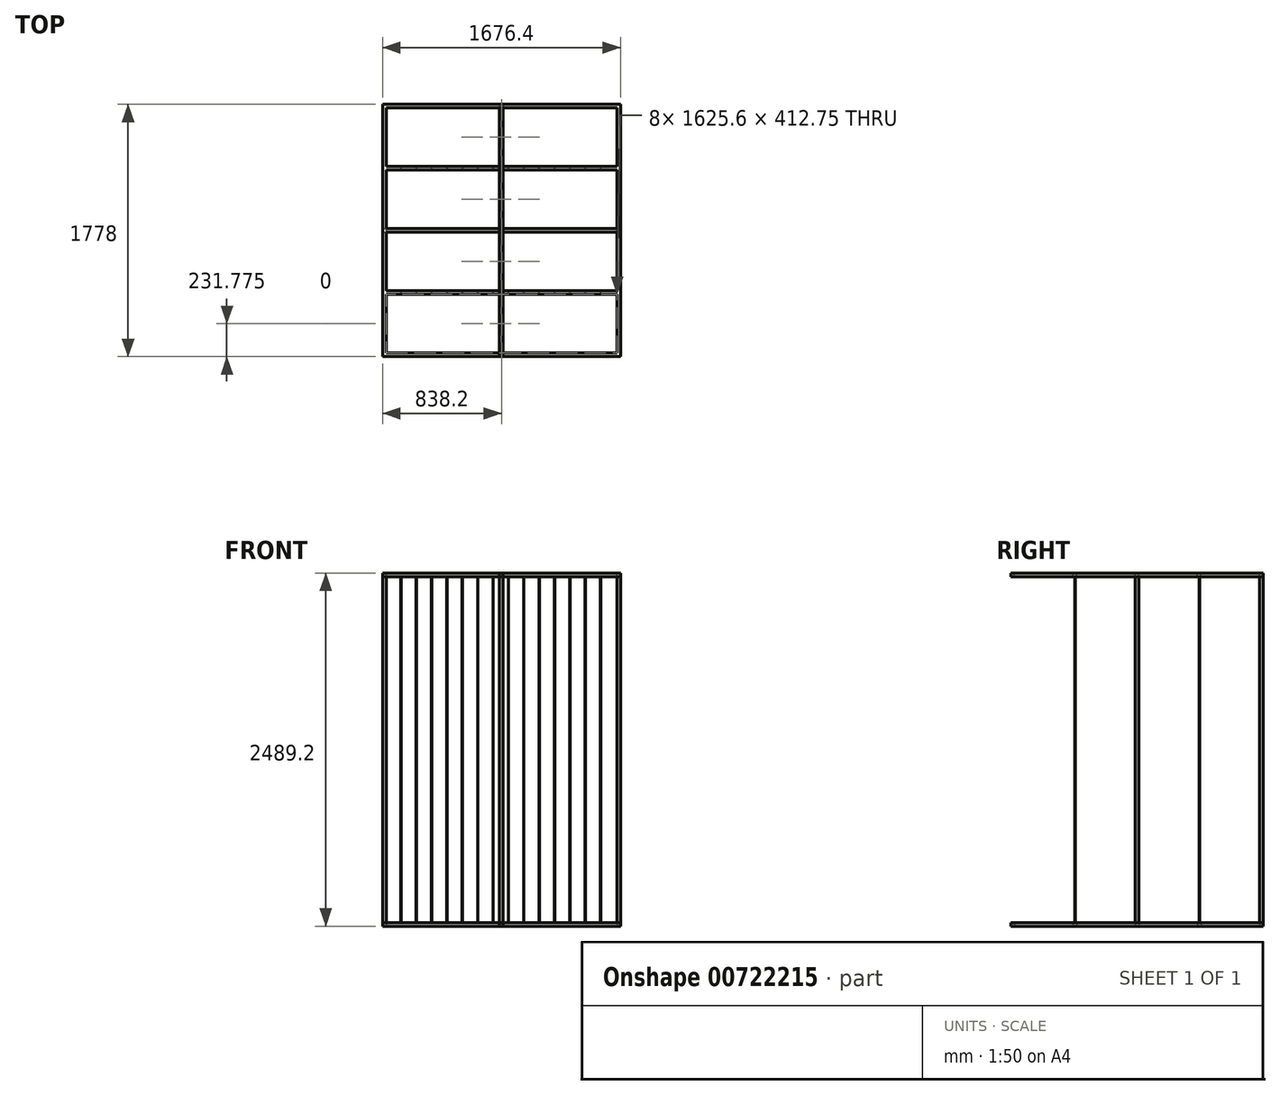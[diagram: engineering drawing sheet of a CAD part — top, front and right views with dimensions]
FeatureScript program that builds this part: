
annotation { "Feature Type Name" : "Feature", "Feature Type Description" : "" }
export const myFeature = defineFeature(function(context is Context, id is Id, definition is map)
    precondition{}
    {
        {
            var Q0;
            Q0=qCreatedBy(makeId("Top.planeOp"),FACE);
            var sketch = newSketch(context, id + "F0", { "sketchPlane" : qUnion([Q0])});
            skLineSegment(sketch, "E0.bottom", {"start": v(838.2, -889) * mm, "end": v(-838.2, -889) * mm});
            skLineSegment(sketch, "E0.top", {"start": v(838.2, 889) * mm, "end": v(-838.2, 889) * mm});
            skLineSegment(sketch, "E0.left", {"start": v(838.2, -889) * mm, "end": v(838.2, 889) * mm});
            skLineSegment(sketch, "E0.right", {"start": v(-838.2, -889) * mm, "end": v(-838.2, 889) * mm});
            skPoint(sketch, "E0.middle", {"position": v(0, 0) * mm});
            skLineSegment(sketch, "E1.0", {"start": v(812.8, 863.6) * mm, "end": v(-812.8, 863.6) * mm});
            skLineSegment(sketch, "E1.1", {"start": v(812.8, -863.6) * mm, "end": v(812.8, -450.85) * mm});
            skLineSegment(sketch, "E1.2", {"start": v(812.8, -863.6) * mm, "end": v(-812.8, -863.6) * mm});
            skLineSegment(sketch, "E1.3", {"start": v(-812.8, -863.6) * mm, "end": v(-812.8, -450.85) * mm});
            skLineSegment(sketch, "E2", {"start": v(-812.8, -450.85) * mm, "end": v(812.8, -450.85) * mm});
            skLineSegment(sketch, "E3", {"start": v(812.8, -425.45) * mm, "end": v(-812.8, -425.45) * mm});
            skLineSegment(sketch, "E4", {"start": v(-812.8, -12.7) * mm, "end": v(812.8, -12.7) * mm});
            skLineSegment(sketch, "E5", {"start": v(-812.8, 0) * mm, "end": v(812.8, 0) * mm, "construction": true});
            skLineSegment(sketch, "E6.MirrorCS", {"start": v(-812.8, 12.7) * mm, "end": v(812.8, 12.7) * mm});
            skLineSegment(sketch, "E7.MirrorCS", {"start": v(812.8, 425.45) * mm, "end": v(-812.8, 425.45) * mm});
            skLineSegment(sketch, "E8.MirrorCS", {"start": v(-812.8, 450.85) * mm, "end": v(812.8, 450.85) * mm});
            skLineSegment(sketch, "E9.trimOffspring", {"start": v(812.8, 450.85) * mm, "end": v(812.8, 863.6) * mm});
            skLineSegment(sketch, "E10.trimOffspring", {"start": v(812.8, 12.7) * mm, "end": v(812.8, 425.45) * mm});
            skLineSegment(sketch, "E11.trimOffspring", {"start": v(812.8, -425.45) * mm, "end": v(812.8, -12.7) * mm});
            skLineSegment(sketch, "E12.trimOffspring", {"start": v(-812.8, -425.45) * mm, "end": v(-812.8, -12.7) * mm});
            skLineSegment(sketch, "E13.trimOffspring", {"start": v(-812.8, 12.7) * mm, "end": v(-812.8, 425.45) * mm});
            skLineSegment(sketch, "E14.trimOffspring", {"start": v(-812.8, 450.85) * mm, "end": v(-812.8, 863.6) * mm});
            skSolve(sketch);
        }
        {
            var Q0;
            Q0 = qSketchRegion(id + "F0", true);
            extrude(context, id + "F1", {"entities" : qUnion([Q0]), "depth" : 25.4 * mm, "offsetDistance" : 25.4 * mm});
        }
        {
            var Q0;
            Q0=qCreatedBy(makeId("Top.planeOp"),FACE);
            cPlane(context, id + "F2", {"entities" : qUnion([Q0]), "cplaneType" : CPlaneType.OFFSET, "offset" : 1244.6 * mm, "width" : 152.4 * mm, "height" : 152.4 * mm});
        }
        {
            var Q0;
            Q0=makeQuery(id+"F1.opExtrude","SWEPT_BODY",BODY,{"disambiguationData":[OSD([sQuery(id+"F0.wireOp",EDGE,"E0.bottom"),sQuery(id+"F0.wireOp",EDGE,"E0.top"),sQuery(id+"F0.wireOp",EDGE,"E0.left"),sQuery(id+"F0.wireOp",EDGE,"E0.right"),sQuery(id+"F0.wireOp",EDGE,"E1.0"),sQuery(id+"F0.wireOp",EDGE,"E1.1"),sQuery(id+"F0.wireOp",EDGE,"E1.2"),sQuery(id+"F0.wireOp",EDGE,"E1.3"),sQuery(id+"F0.wireOp",EDGE,"E2"),sQuery(id+"F0.wireOp",EDGE,"E3"),sQuery(id+"F0.wireOp",EDGE,"E4"),sQuery(id+"F0.wireOp",EDGE,"E6.MirrorCS"),sQuery(id+"F0.wireOp",EDGE,"E7.MirrorCS"),sQuery(id+"F0.wireOp",EDGE,"E8.MirrorCS"),sQuery(id+"F0.wireOp",EDGE,"E9.trimOffspring"),sQuery(id+"F0.wireOp",EDGE,"E10.trimOffspring"),sQuery(id+"F0.wireOp",EDGE,"E11.trimOffspring"),sQuery(id+"F0.wireOp",EDGE,"E12.trimOffspring"),sQuery(id+"F0.wireOp",EDGE,"E13.trimOffspring"),sQuery(id+"F0.wireOp",EDGE,"E14.trimOffspring")])]});
            var Q1;
            Q1=qCreatedBy(id+"F2.planeOp",FACE);
            mirror(context, id + "F3", {"entities" : qUnion([Q0]), "mirrorPlane" : qUnion([Q1])});
        }
        {
            var Q0;
            Q0=makeQuery(id+"F1.opExtrude","CAP_FACE",FACE,{"disambiguationData":[OSD([sQuery(id+"F0.wireOp",EDGE,"E0.bottom"),sQuery(id+"F0.wireOp",EDGE,"E0.top"),sQuery(id+"F0.wireOp",EDGE,"E0.left"),sQuery(id+"F0.wireOp",EDGE,"E0.right"),sQuery(id+"F0.wireOp",EDGE,"E1.0"),sQuery(id+"F0.wireOp",EDGE,"E1.1"),sQuery(id+"F0.wireOp",EDGE,"E1.2"),sQuery(id+"F0.wireOp",EDGE,"E1.3"),sQuery(id+"F0.wireOp",EDGE,"E2"),sQuery(id+"F0.wireOp",EDGE,"E3"),sQuery(id+"F0.wireOp",EDGE,"E4"),sQuery(id+"F0.wireOp",EDGE,"E6.MirrorCS"),sQuery(id+"F0.wireOp",EDGE,"E7.MirrorCS"),sQuery(id+"F0.wireOp",EDGE,"E8.MirrorCS"),sQuery(id+"F0.wireOp",EDGE,"E9.trimOffspring"),sQuery(id+"F0.wireOp",EDGE,"E10.trimOffspring"),sQuery(id+"F0.wireOp",EDGE,"E11.trimOffspring"),sQuery(id+"F0.wireOp",EDGE,"E12.trimOffspring"),sQuery(id+"F0.wireOp",EDGE,"E13.trimOffspring"),sQuery(id+"F0.wireOp",EDGE,"E14.trimOffspring")])],"isStart":false});
            var sketch = newSketch(context, id + "F4", { "sketchPlane" : qUnion([Q0])});
            skLineSegment(sketch, "E15.0", {"start": v(838.2, 889) * mm, "end": v(-838.2, 889) * mm});
            skLineSegment(sketch, "E15.1", {"start": v(-838.2, -889) * mm, "end": v(-838.2, 889) * mm});
            skLineSegment(sketch, "E15.2", {"start": v(838.2, -889) * mm, "end": v(838.2, 889) * mm});
            skLineSegment(sketch, "E15.3", {"start": v(838.2, -889) * mm, "end": v(-838.2, -889) * mm});
            skLineSegment(sketch, "E16.bottom", {"start": v(-838.2, -889) * mm, "end": v(-812.8, -889) * mm});
            skLineSegment(sketch, "E16.top", {"start": v(-838.2, -863.6) * mm, "end": v(-812.8, -863.6) * mm});
            skLineSegment(sketch, "E16.left", {"start": v(-838.2, -889) * mm, "end": v(-838.2, -863.6) * mm});
            skLineSegment(sketch, "E16.right", {"start": v(-812.8, -889) * mm, "end": v(-812.8, -863.6) * mm});
            skLineSegment(sketch, "E17.bottom", {"start": v(838.2, -889) * mm, "end": v(812.8, -889) * mm});
            skLineSegment(sketch, "E17.top", {"start": v(838.2, -863.6) * mm, "end": v(812.8, -863.6) * mm});
            skLineSegment(sketch, "E17.left", {"start": v(838.2, -889) * mm, "end": v(838.2, -863.6) * mm});
            skLineSegment(sketch, "E17.right", {"start": v(812.8, -889) * mm, "end": v(812.8, -863.6) * mm});
            skLineSegment(sketch, "E18.bottom", {"start": v(-838.2, 889) * mm, "end": v(-812.8, 889) * mm});
            skLineSegment(sketch, "E18.top", {"start": v(-838.2, 863.6) * mm, "end": v(-812.8, 863.6) * mm});
            skLineSegment(sketch, "E18.left", {"start": v(-838.2, 889) * mm, "end": v(-838.2, 863.6) * mm});
            skLineSegment(sketch, "E18.right", {"start": v(-812.8, 889) * mm, "end": v(-812.8, 863.6) * mm});
            skLineSegment(sketch, "E19.bottom", {"start": v(838.2, 889) * mm, "end": v(812.8, 889) * mm});
            skLineSegment(sketch, "E19.top", {"start": v(838.2, 863.6) * mm, "end": v(812.8, 863.6) * mm});
            skLineSegment(sketch, "E19.left", {"start": v(838.2, 889) * mm, "end": v(838.2, 863.6) * mm});
            skLineSegment(sketch, "E19.right", {"start": v(812.8, 889) * mm, "end": v(812.8, 863.6) * mm});
            skLineSegment(sketch, "E20.bottom", {"start": v(-812.8, 12.7) * mm, "end": v(-838.2, 12.7) * mm});
            skLineSegment(sketch, "E20.top", {"start": v(-812.8, -12.7) * mm, "end": v(-838.2, -12.7) * mm});
            skLineSegment(sketch, "E20.left", {"start": v(-812.8, 12.7) * mm, "end": v(-812.8, -12.7) * mm});
            skLineSegment(sketch, "E20.right", {"start": v(-838.2, 12.7) * mm, "end": v(-838.2, -12.7) * mm});
            skLineSegment(sketch, "E21.bottom", {"start": v(812.8, 12.7) * mm, "end": v(838.2, 12.7) * mm});
            skLineSegment(sketch, "E21.top", {"start": v(812.8, -12.7) * mm, "end": v(838.2, -12.7) * mm});
            skLineSegment(sketch, "E21.left", {"start": v(812.8, 12.7) * mm, "end": v(812.8, -12.7) * mm});
            skLineSegment(sketch, "E21.right", {"start": v(838.2, 12.7) * mm, "end": v(838.2, -12.7) * mm});
            skLineSegment(sketch, "E22.bottom", {"start": v(-12.7, 863.6) * mm, "end": v(12.7, 863.6) * mm});
            skLineSegment(sketch, "E22.top", {"start": v(-12.7, 889) * mm, "end": v(12.7, 889) * mm});
            skLineSegment(sketch, "E22.left", {"start": v(-12.7, 863.6) * mm, "end": v(-12.7, 889) * mm});
            skLineSegment(sketch, "E22.right", {"start": v(12.7, 863.6) * mm, "end": v(12.7, 889) * mm});
            skPoint(sketch, "E22.middle", {"position": v(0, 876.3) * mm});
            skPoint(sketch, "E22.middle.positionSnap0", {"position": v(0, 889) * mm});
            skPoint(sketch, "E22.middle.positionSnap1", {"position": v(-812.8, 876.3) * mm});
            skPoint(sketch, "E22.centerSnap0", {"position": v(0, 889) * mm});
            skPoint(sketch, "E22.centerSnap1", {"position": v(-812.8, 876.3) * mm});
            skLineSegment(sketch, "E23.bottom", {"start": v(-12.7, -889) * mm, "end": v(12.7, -889) * mm});
            skLineSegment(sketch, "E23.top", {"start": v(-12.7, -863.6) * mm, "end": v(12.7, -863.6) * mm});
            skLineSegment(sketch, "E23.left", {"start": v(-12.7, -889) * mm, "end": v(-12.7, -863.6) * mm});
            skLineSegment(sketch, "E23.right", {"start": v(12.7, -889) * mm, "end": v(12.7, -863.6) * mm});
            skPoint(sketch, "E23.middle", {"position": v(0, -876.3) * mm});
            skPoint(sketch, "E23.middle.positionSnap0", {"position": v(0, -889) * mm});
            skPoint(sketch, "E23.middle.positionSnap1", {"position": v(-812.8, -876.3) * mm});
            skPoint(sketch, "E23.centerSnap0", {"position": v(0, -889) * mm});
            skPoint(sketch, "E23.centerSnap1", {"position": v(-812.8, -876.3) * mm});
            skSolve(sketch);
        }
        {
            var Q0;
            Q0=makeQuery(id+"F4.imprint","IMPRINT",FACE,{"disambiguationData":[TD([[makeQuery(id+"F4.imprint","IMPRINT",EDGE,{"derivedFrom":sQuery(id+"F4.wireOp",EDGE,"E20.bottom")}),1.0]])]});
            var Q1;
            Q1=makeQuery(id+"F4.imprint","IMPRINT",FACE,{"disambiguationData":[TD([[makeQuery(id+"F4.imprint","IMPRINT",EDGE,{"derivedFrom":sQuery(id+"F4.wireOp",EDGE,"E18.bottom")}),1.0]])]});
            var Q2;
            Q2=makeQuery(id+"F4.imprint","IMPRINT",FACE,{"disambiguationData":[TD([[makeQuery(id+"F4.imprint","IMPRINT",EDGE,{"derivedFrom":sQuery(id+"F4.wireOp",EDGE,"E22.bottom")}),-1.0]])]});
            var Q3;
            Q3=makeQuery(id+"F4.imprint","IMPRINT",FACE,{"disambiguationData":[TD([[makeQuery(id+"F4.imprint","IMPRINT",EDGE,{"derivedFrom":sQuery(id+"F4.wireOp",EDGE,"E19.bottom")}),1.0]])]});
            var Q4;
            Q4=makeQuery(id+"F4.imprint","IMPRINT",FACE,{"disambiguationData":[TD([[makeQuery(id+"F4.imprint","IMPRINT",EDGE,{"derivedFrom":sQuery(id+"F4.wireOp",EDGE,"E21.bottom")}),-1.0]])]});
            var Q5;
            Q5=makeQuery(id+"F4.imprint","IMPRINT",FACE,{"disambiguationData":[TD([[makeQuery(id+"F4.imprint","IMPRINT",EDGE,{"derivedFrom":sQuery(id+"F4.wireOp",EDGE,"E17.bottom")}),-1.0]])]});
            var Q6;
            Q6=makeQuery(id+"F4.imprint","IMPRINT",FACE,{"disambiguationData":[TD([[makeQuery(id+"F4.imprint","IMPRINT",EDGE,{"derivedFrom":sQuery(id+"F4.wireOp",EDGE,"E23.bottom")}),-1.0]])]});
            var Q7;
            Q7=makeQuery(id+"F4.imprint","IMPRINT",FACE,{"disambiguationData":[TD([[makeQuery(id+"F4.imprint","IMPRINT",EDGE,{"derivedFrom":sQuery(id+"F4.wireOp",EDGE,"E16.bottom")}),-1.0]])]});
            var Q8;
            Q8=makeQuery(id+"F1.opExtrude","CAP_FACE",FACE,{"disambiguationData":[OSD([sQuery(id+"F0.wireOp",EDGE,"E0.bottom"),sQuery(id+"F0.wireOp",EDGE,"E0.top"),sQuery(id+"F0.wireOp",EDGE,"E0.left"),sQuery(id+"F0.wireOp",EDGE,"E0.right"),sQuery(id+"F0.wireOp",EDGE,"E1.0"),sQuery(id+"F0.wireOp",EDGE,"E1.1"),sQuery(id+"F0.wireOp",EDGE,"E1.2"),sQuery(id+"F0.wireOp",EDGE,"E1.3"),sQuery(id+"F0.wireOp",EDGE,"E2"),sQuery(id+"F0.wireOp",EDGE,"E3"),sQuery(id+"F0.wireOp",EDGE,"E4"),sQuery(id+"F0.wireOp",EDGE,"E6.MirrorCS"),sQuery(id+"F0.wireOp",EDGE,"E7.MirrorCS"),sQuery(id+"F0.wireOp",EDGE,"E8.MirrorCS"),sQuery(id+"F0.wireOp",EDGE,"E9.trimOffspring"),sQuery(id+"F0.wireOp",EDGE,"E10.trimOffspring"),sQuery(id+"F0.wireOp",EDGE,"E11.trimOffspring"),sQuery(id+"F0.wireOp",EDGE,"E12.trimOffspring"),sQuery(id+"F0.wireOp",EDGE,"E13.trimOffspring"),sQuery(id+"F0.wireOp",EDGE,"E14.trimOffspring")])],"isStart":false});
            var Q9;
            Q9=makeQuery(id+"F3.opPattern","COPY",BODY,{"derivedFrom":makeQuery(id+"F1.opExtrude","SWEPT_BODY",BODY,{"disambiguationData":[OSD([sQuery(id+"F0.wireOp",EDGE,"E0.bottom"),sQuery(id+"F0.wireOp",EDGE,"E0.top"),sQuery(id+"F0.wireOp",EDGE,"E0.left"),sQuery(id+"F0.wireOp",EDGE,"E0.right"),sQuery(id+"F0.wireOp",EDGE,"E1.0"),sQuery(id+"F0.wireOp",EDGE,"E1.1"),sQuery(id+"F0.wireOp",EDGE,"E1.2"),sQuery(id+"F0.wireOp",EDGE,"E1.3"),sQuery(id+"F0.wireOp",EDGE,"E2"),sQuery(id+"F0.wireOp",EDGE,"E3"),sQuery(id+"F0.wireOp",EDGE,"E4"),sQuery(id+"F0.wireOp",EDGE,"E6.MirrorCS"),sQuery(id+"F0.wireOp",EDGE,"E7.MirrorCS"),sQuery(id+"F0.wireOp",EDGE,"E8.MirrorCS"),sQuery(id+"F0.wireOp",EDGE,"E9.trimOffspring"),sQuery(id+"F0.wireOp",EDGE,"E10.trimOffspring"),sQuery(id+"F0.wireOp",EDGE,"E11.trimOffspring"),sQuery(id+"F0.wireOp",EDGE,"E12.trimOffspring"),sQuery(id+"F0.wireOp",EDGE,"E13.trimOffspring"),sQuery(id+"F0.wireOp",EDGE,"E14.trimOffspring")])]}),"instanceName":"1"});
            extrude(context, id + "F5", {"entities" : qUnion([Q0, Q1, Q2, Q3, Q4, Q5, Q6, Q7]), "endBound" : BoundingType.UP_TO_BODY, "depth" : 25.4 * mm, "endBoundEntityFace" : qUnion([Q8]), "endBoundEntityBody" : qUnion([Q9]), "offsetDistance" : 25.4 * mm});
        }
        {
            var Q0;
            Q0=makeQuery(id+"F1.opExtrude","SWEPT_FACE",FACE,{"disambiguationData":[OSD([sQuery(id+"F0.wireOp",EDGE,"E0.bottom")])]});
            var sketch = newSketch(context, id + "F6", { "sketchPlane" : qUnion([Q0])});
            skLineSegment(sketch, "E24", {"start": v(0, 0) * mm, "end": v(0, 25.4) * mm, "construction": true});
            skLineSegment(sketch, "E25", {"start": v(-12.7, 0) * mm, "end": v(-12.7, 25.4) * mm});
            skLineSegment(sketch, "E26.MirrorCS", {"start": v(12.7, 0) * mm, "end": v(12.7, 25.4) * mm});
            skLineSegment(sketch, "E27", {"start": v(-12.7, 25.4) * mm, "end": v(12.7, 25.4) * mm});
            skLineSegment(sketch, "E28", {"start": v(-12.7, 0) * mm, "end": v(12.7, 0) * mm});
            skSolve(sketch);
        }
        {
            var Q0;
            Q0 = qSketchRegion(id + "F6", true);
            var Q1;
            Q1=makeQuery(id+"F1.opExtrude","SWEPT_FACE",FACE,{"disambiguationData":[OSD([sQuery(id+"F0.wireOp",EDGE,"E1.0")])]});
            extrude(context, id + "F7", {"entities" : qUnion([Q0]), "endBound" : BoundingType.UP_TO_SURFACE, "oppositeDirection" : true, "depth" : 25.4 * mm, "endBoundEntityFace" : qUnion([Q1]), "offsetDistance" : 25.4 * mm});
        }
        {
            var Q0;
            Q0=makeQuery(id+"F7.opExtrude","SWEPT_BODY",BODY,{"disambiguationData":[OSD([sQuery(id+"F6.wireOp",EDGE,"E25"),sQuery(id+"F6.wireOp",EDGE,"E26.MirrorCS"),sQuery(id+"F6.wireOp",EDGE,"E27"),sQuery(id+"F6.wireOp",EDGE,"E28")])]});
            var Q1;
            Q1=qCreatedBy(id+"F2.planeOp",FACE);
            mirror(context, id + "F8", {"entities" : qUnion([Q0]), "mirrorPlane" : qUnion([Q1])});
        }
        {
            var Q0;
            Q0=makeQuery(id+"F1.opExtrude","CAP_FACE",FACE,{"disambiguationData":[OSD([sQuery(id+"F0.wireOp",EDGE,"E0.bottom"),sQuery(id+"F0.wireOp",EDGE,"E0.top"),sQuery(id+"F0.wireOp",EDGE,"E0.left"),sQuery(id+"F0.wireOp",EDGE,"E0.right"),sQuery(id+"F0.wireOp",EDGE,"E1.0"),sQuery(id+"F0.wireOp",EDGE,"E1.1"),sQuery(id+"F0.wireOp",EDGE,"E1.2"),sQuery(id+"F0.wireOp",EDGE,"E1.3"),sQuery(id+"F0.wireOp",EDGE,"E2"),sQuery(id+"F0.wireOp",EDGE,"E3"),sQuery(id+"F0.wireOp",EDGE,"E4"),sQuery(id+"F0.wireOp",EDGE,"E6.MirrorCS"),sQuery(id+"F0.wireOp",EDGE,"E7.MirrorCS"),sQuery(id+"F0.wireOp",EDGE,"E8.MirrorCS"),sQuery(id+"F0.wireOp",EDGE,"E9.trimOffspring"),sQuery(id+"F0.wireOp",EDGE,"E10.trimOffspring"),sQuery(id+"F0.wireOp",EDGE,"E11.trimOffspring"),sQuery(id+"F0.wireOp",EDGE,"E12.trimOffspring"),sQuery(id+"F0.wireOp",EDGE,"E13.trimOffspring"),sQuery(id+"F0.wireOp",EDGE,"E14.trimOffspring")])],"isStart":false});
            var sketch = newSketch(context, id + "F9", { "sketchPlane" : qUnion([Q0])});
            skLineSegment(sketch, "E29.0", {"start": v(812.8, -425.45) * mm, "end": v(-812.8, -425.45) * mm, "construction": true});
            skLineSegment(sketch, "E29.1", {"start": v(-812.8, -450.85) * mm, "end": v(812.8, -450.85) * mm, "construction": true});
            skLineSegment(sketch, "E30", {"start": v(-812.8, -425.45) * mm, "end": v(-812.8, -450.85) * mm, "construction": true});
            skCircle(sketch, "E31", {"center": v(-708.02, -438.15) * mm, "radius": 1.02 * mm});
            skPoint(sketch, "E31.centerSnap0", {"position": v(-812.8, -438.15) * mm});
            skCircle(sketch, "E32.1.0.0", {"center": v(-599.82, -438.15) * mm, "radius": 1.02 * mm});
            skCircle(sketch, "E32.2.0.0", {"center": v(-491.62, -438.15) * mm, "radius": 1.02 * mm});
            skCircle(sketch, "E32.3.0.0", {"center": v(-383.41, -438.15) * mm, "radius": 1.02 * mm});
            skCircle(sketch, "E32.4.0.0", {"center": v(-275.2, -438.15) * mm, "radius": 1.02 * mm});
            skCircle(sketch, "E32.5.0.0", {"center": v(-167, -438.15) * mm, "radius": 1.02 * mm});
            skCircle(sketch, "E32.6.0.0", {"center": v(-58.8, -438.15) * mm, "radius": 1.02 * mm});
            skCircle(sketch, "E32.7.0.0", {"center": v(49.4, -438.15) * mm, "radius": 1.02 * mm});
            skCircle(sketch, "E32.8.0.0", {"center": v(157.6, -438.15) * mm, "radius": 1.02 * mm});
            skCircle(sketch, "E32.9.0.0", {"center": v(265.81, -438.15) * mm, "radius": 1.02 * mm});
            skCircle(sketch, "E32.10.0.0", {"center": v(374.01, -438.15) * mm, "radius": 1.02 * mm});
            skCircle(sketch, "E32.11.0.0", {"center": v(482.22, -438.15) * mm, "radius": 1.02 * mm});
            skCircle(sketch, "E32.12.0.0", {"center": v(590.42, -438.15) * mm, "radius": 1.02 * mm});
            skCircle(sketch, "E32.13.0.0", {"center": v(698.63, -438.15) * mm, "radius": 1.02 * mm});
            skLineSegment(sketch, "E32.direction1", {"start": v(-708.02, -438.15) * mm, "end": v(-599.82, -438.15) * mm, "construction": true});
            skSolve(sketch);
        }
        {
            var Q0;
            Q0 = qSketchRegion(id + "F9", true);
            var Q1;
            Q1=makeQuery(id+"F3.opPattern","COPY",FACE,{"derivedFrom":makeQuery(id+"F1.opExtrude","CAP_FACE",FACE,{"disambiguationData":[OSD([sQuery(id+"F0.wireOp",EDGE,"E0.bottom"),sQuery(id+"F0.wireOp",EDGE,"E0.top"),sQuery(id+"F0.wireOp",EDGE,"E0.left"),sQuery(id+"F0.wireOp",EDGE,"E0.right"),sQuery(id+"F0.wireOp",EDGE,"E1.0"),sQuery(id+"F0.wireOp",EDGE,"E1.1"),sQuery(id+"F0.wireOp",EDGE,"E1.2"),sQuery(id+"F0.wireOp",EDGE,"E1.3"),sQuery(id+"F0.wireOp",EDGE,"E2"),sQuery(id+"F0.wireOp",EDGE,"E3"),sQuery(id+"F0.wireOp",EDGE,"E4"),sQuery(id+"F0.wireOp",EDGE,"E6.MirrorCS"),sQuery(id+"F0.wireOp",EDGE,"E7.MirrorCS"),sQuery(id+"F0.wireOp",EDGE,"E8.MirrorCS"),sQuery(id+"F0.wireOp",EDGE,"E9.trimOffspring"),sQuery(id+"F0.wireOp",EDGE,"E10.trimOffspring"),sQuery(id+"F0.wireOp",EDGE,"E11.trimOffspring"),sQuery(id+"F0.wireOp",EDGE,"E12.trimOffspring"),sQuery(id+"F0.wireOp",EDGE,"E13.trimOffspring"),sQuery(id+"F0.wireOp",EDGE,"E14.trimOffspring")])],"isStart":false}),"instanceName":"1"});
            extrude(context, id + "F10", {"entities" : qUnion([Q0]), "endBound" : BoundingType.UP_TO_SURFACE, "depth" : 25.4 * mm, "endBoundEntityFace" : qUnion([Q1]), "offsetDistance" : 25.4 * mm});
        }
        {
            var Q0;
            Q0=makeQuery(id+"F10.opExtrude","SWEPT_BODY",BODY,{"disambiguationData":[OSD([sQuery(id+"F9.wireOp",EDGE,"E32.1.0.0")])]});
            var Q1;
            Q1=makeQuery(id+"F10.opExtrude","SWEPT_BODY",BODY,{"disambiguationData":[OSD([sQuery(id+"F9.wireOp",EDGE,"E31")])]});
            var Q2;
            Q2=makeQuery(id+"F10.opExtrude","SWEPT_BODY",BODY,{"disambiguationData":[OSD([sQuery(id+"F9.wireOp",EDGE,"E32.2.0.0")])]});
            var Q3;
            Q3=makeQuery(id+"F10.opExtrude","SWEPT_BODY",BODY,{"disambiguationData":[OSD([sQuery(id+"F9.wireOp",EDGE,"E32.3.0.0")])]});
            var Q4;
            Q4=makeQuery(id+"F10.opExtrude","SWEPT_BODY",BODY,{"disambiguationData":[OSD([sQuery(id+"F9.wireOp",EDGE,"E32.4.0.0")])]});
            var Q5;
            Q5=makeQuery(id+"F10.opExtrude","SWEPT_BODY",BODY,{"disambiguationData":[OSD([sQuery(id+"F9.wireOp",EDGE,"E32.5.0.0")])]});
            var Q6;
            Q6=makeQuery(id+"F10.opExtrude","SWEPT_BODY",BODY,{"disambiguationData":[OSD([sQuery(id+"F9.wireOp",EDGE,"E32.6.0.0")])]});
            var Q7;
            Q7=makeQuery(id+"F10.opExtrude","SWEPT_BODY",BODY,{"disambiguationData":[OSD([sQuery(id+"F9.wireOp",EDGE,"E32.7.0.0")])]});
            var Q8;
            Q8=makeQuery(id+"F10.opExtrude","SWEPT_BODY",BODY,{"disambiguationData":[OSD([sQuery(id+"F9.wireOp",EDGE,"E32.8.0.0")])]});
            var Q9;
            Q9=makeQuery(id+"F10.opExtrude","SWEPT_BODY",BODY,{"disambiguationData":[OSD([sQuery(id+"F9.wireOp",EDGE,"E32.9.0.0")])]});
            var Q10;
            Q10=makeQuery(id+"F10.opExtrude","SWEPT_BODY",BODY,{"disambiguationData":[OSD([sQuery(id+"F9.wireOp",EDGE,"E32.10.0.0")])]});
            var Q11;
            Q11=makeQuery(id+"F10.opExtrude","SWEPT_BODY",BODY,{"disambiguationData":[OSD([sQuery(id+"F9.wireOp",EDGE,"E32.11.0.0")])]});
            var Q12;
            Q12=makeQuery(id+"F10.opExtrude","SWEPT_BODY",BODY,{"disambiguationData":[OSD([sQuery(id+"F9.wireOp",EDGE,"E32.12.0.0")])]});
            var Q13;
            Q13=makeQuery(id+"F10.opExtrude","SWEPT_BODY",BODY,{"disambiguationData":[OSD([sQuery(id+"F9.wireOp",EDGE,"E32.13.0.0")])]});
            var Q14;
            Q14=qCreatedBy(makeId("Front.planeOp"),FACE);
            mirror(context, id + "F11", {"entities" : qUnion([Q0, Q1, Q2, Q3, Q4, Q5, Q6, Q7, Q8, Q9, Q10, Q11, Q12, Q13]), "mirrorPlane" : qUnion([Q14])});
        }
    });
